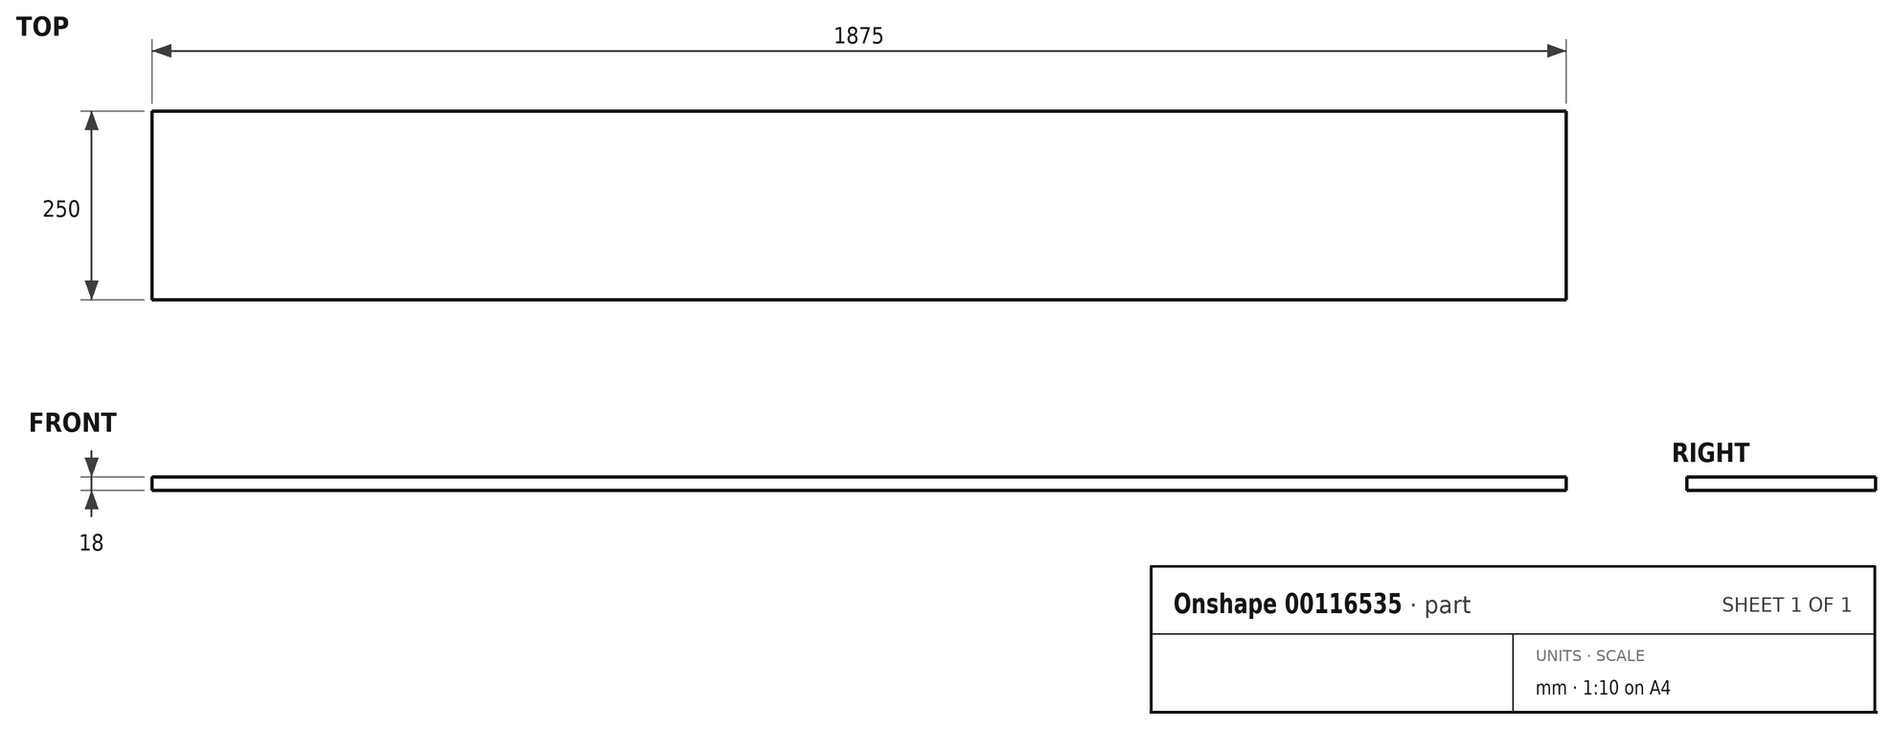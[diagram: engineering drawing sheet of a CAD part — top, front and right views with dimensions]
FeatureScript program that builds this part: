
annotation { "Feature Type Name" : "Feature", "Feature Type Description" : "" }
export const myFeature = defineFeature(function(context is Context, id is Id, definition is map)
    precondition{}
    {
        {
            var Q0;
            Q0=qCreatedBy(makeId("Top.planeOp"),FACE);
            var sketch = newSketch(context, id + "F0", { "sketchPlane" : qUnion([Q0])});
            skLineSegment(sketch, "E0.bottom", {"start": v(-57.48, 285.12) * mm, "end": v(417.52, 285.12) * mm});
            skLineSegment(sketch, "E0.top", {"start": v(-57.48, 35.12) * mm, "end": v(417.52, 35.12) * mm});
            skLineSegment(sketch, "E0.left", {"start": v(-57.48, 285.12) * mm, "end": v(-57.48, 35.12) * mm});
            skLineSegment(sketch, "E0.right", {"start": v(417.52, 285.12) * mm, "end": v(417.52, 35.12) * mm});
            skLineSegment(sketch, "E1", {"start": v(-57.48, 285.12) * mm, "end": v(62.74, 164.91) * mm});
            skLineSegment(sketch, "E2", {"start": v(62.74, 164.91) * mm, "end": v(192.52, 35.12) * mm});
            skLineSegment(sketch, "E3.bottom", {"start": v(-57.48, 285.12) * mm, "end": v(-1457.48, 285.12) * mm});
            skLineSegment(sketch, "E3.top", {"start": v(-57.48, 35.12) * mm, "end": v(-1457.48, 35.12) * mm});
            skLineSegment(sketch, "E3.right", {"start": v(-1457.48, 285.12) * mm, "end": v(-1457.48, 35.12) * mm});
            skLineSegment(sketch, "E4.bottom", {"start": v(-1457.48, 285.12) * mm, "end": v(-1717.48, 285.12) * mm});
            skLineSegment(sketch, "E4.top", {"start": v(-1457.48, 35.12) * mm, "end": v(-1717.48, 35.12) * mm});
            skLineSegment(sketch, "E4.right", {"start": v(-1717.48, 285.12) * mm, "end": v(-1717.48, 35.12) * mm});
            skLineSegment(sketch, "E5.bottom", {"start": v(417.52, 285.12) * mm, "end": v(852.52, 285.12) * mm});
            skLineSegment(sketch, "E5.top", {"start": v(417.52, 35.12) * mm, "end": v(852.52, 35.12) * mm});
            skLineSegment(sketch, "E5.right", {"start": v(852.52, 285.12) * mm, "end": v(852.52, 35.12) * mm});
            skSolve(sketch);
        }
        {
            var Q0;
            {var subQ0=sQuery(id+"F0.wireOp",EDGE,"E0.left");Q0=makeQuery(id+"F0.imprint","IMPRINT",FACE,{"disambiguationData":[TD([[makeQuery(id+"F0.imprint","IMPRINT",EDGE,{"derivedFrom":subQ0}),1.0]])]});}
            var Q1;
            Q1=makeQuery(id+"F0.imprint","IMPRINT",FACE,{"disambiguationData":[TD([[makeQuery(id+"F0.imprint","IMPRINT",EDGE,{"derivedFrom":sQuery(id+"F0.wireOp",EDGE,"E3.bottom")}),1.0]])]});
            var Q2;
            Q2=makeQuery(id+"F0.imprint","IMPRINT",FACE,{"disambiguationData":[TD([[makeQuery(id+"F0.imprint","IMPRINT",EDGE,{"derivedFrom":sQuery(id+"F0.wireOp",EDGE,"E0.bottom")}),-1.0]])]});
            var Q3;
            Q3=makeQuery(id+"F0.imprint","IMPRINT",FACE,{"disambiguationData":[TD([[makeQuery(id+"F0.imprint","IMPRINT",EDGE,{"derivedFrom":sQuery(id+"F0.wireOp",EDGE,"E1")}),-1.0]])]});
            extrude(context, id + "F1", {"entities" : qUnion([Q0, Q1, Q2, Q3]), "depth" : 18 * mm});
        }
    });
